# Revit family: BTWASP
name_source: partatom
category: Communication Devices
units: mm (PartAtom-declared; Revit-internal decimal feet)

## family parameters
Cut with Voids When Loaded = No
Host = Face
Maintain Annotation Orientation = No
OmniClass Number = 23.85.80.11.27
OmniClass Title = Lighting Controls
Part Type = Normal
Room Calculation Point = No
Round Connector Dimension = Use Diameter
Shared = Yes

## types (1)
- BTWASP
    Assembly Code = D5090
    Certifications = Conforms with UL STD 508, UL STD 244A
• LWO version conforms to IP65
    Coverage = 360°, 180°, Aisle, Half Aisle
    Default Elevation = 48 "
    Description = BLUETOOTH® WASP SENSOR OCCUPANCY/VACANCY SENSORS AND CONTROLLERS
    Features = Wireless programming using HCS Control Bluetooth app
• ON/OFF and 0-10V dimming control
• Single/Dual motion sensor timer modes
• Multiple daylight harvesting modes for indoor and outdoor applications
• Interchangeable high/low area detection lens options
• Low voltage and line voltage models available
• Daylight sensor for daylight harvesting applications
• Low temperature/water-tight/indoor-outdoor versions
    Housing Material = Paint - Matte White
    Manufacturer = NX Lighting Controls
    Model = BTWASP
    Power Requirements = Line Voltage sensors: 120/277/347VAC, 60 Hz
    Sensing Element = Glass -  White
    Type Comments = Occupancy/ Vacancy Sensors and Controllers
    URL = https://www.currentlighting.com
    Warranty = 5-Years Warranty
    Width = 4 "

## geometry (parser evidence)
native form markers: Sweep x3
no freeform markers — native parametric forms only
